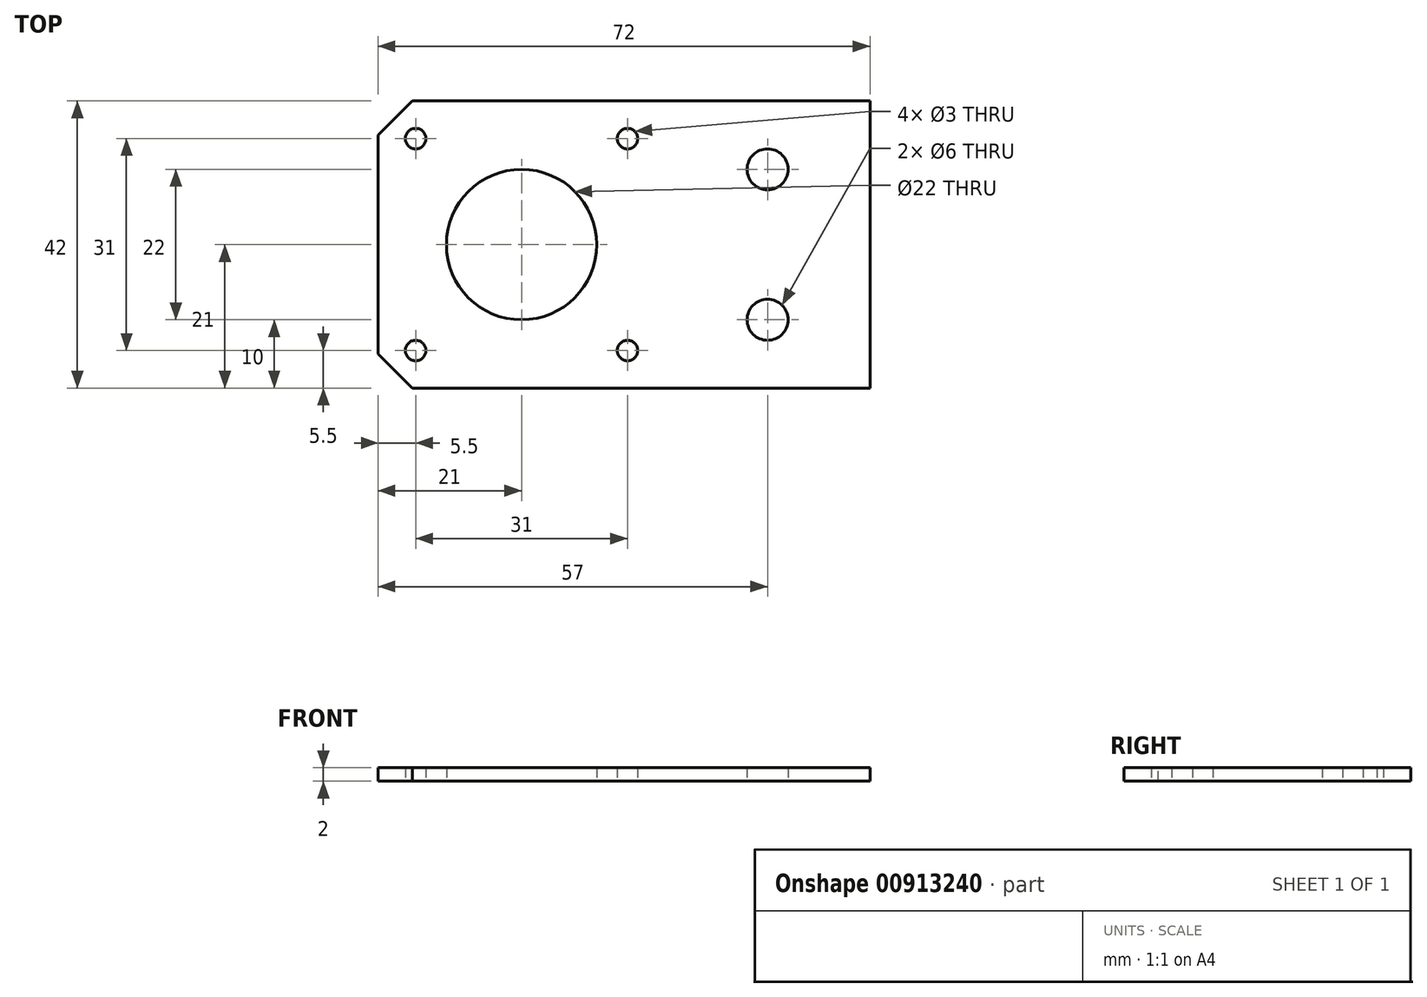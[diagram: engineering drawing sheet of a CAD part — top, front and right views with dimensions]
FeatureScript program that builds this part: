
annotation { "Feature Type Name" : "Feature", "Feature Type Description" : "" }
export const myFeature = defineFeature(function(context is Context, id is Id, definition is map)
    precondition{}
    {
        {
            var Q0;
            Q0=qCreatedBy(makeId("Top.planeOp"),FACE);
            var sketch = newSketch(context, id + "F0", { "sketchPlane" : qUnion([Q0])});
            skLineSegment(sketch, "E0.bottom", {"start": v(36, -21) * mm, "end": v(-36, -21) * mm});
            skLineSegment(sketch, "E0.top", {"start": v(36, 21) * mm, "end": v(-36, 21) * mm});
            skLineSegment(sketch, "E0.left", {"start": v(36, -21) * mm, "end": v(36, 21) * mm});
            skLineSegment(sketch, "E0.right", {"start": v(-36, -21) * mm, "end": v(-36, 21) * mm});
            skPoint(sketch, "E0.middle", {"position": v(0, 0) * mm});
            skCircle(sketch, "E1", {"center": v(21, 11) * mm, "radius": 3 * mm});
            skCircle(sketch, "E2", {"center": v(21, -11) * mm, "radius": 3 * mm});
            skCircle(sketch, "E3", {"center": v(-15, 0) * mm, "radius": 11 * mm});
            skCircle(sketch, "E4", {"center": v(-30.5, 15.5) * mm, "radius": 1.5 * mm});
            skCircle(sketch, "E5", {"center": v(0.5, 15.5) * mm, "radius": 1.5 * mm});
            skCircle(sketch, "E6", {"center": v(0.5, -15.5) * mm, "radius": 1.5 * mm});
            skCircle(sketch, "E7", {"center": v(-30.5, -15.5) * mm, "radius": 1.5 * mm});
            skSolve(sketch);
        }
        {
            var Q0;
            Q0=makeQuery(id+"F0.imprint","IMPRINT",FACE,{"disambiguationData":[TD([[makeQuery(id+"F0.imprint","IMPRINT",EDGE,{"derivedFrom":sQuery(id+"F0.wireOp",EDGE,"E0.bottom")}),-1.0]])]});
            extrude(context, id + "F1", {"entities" : qUnion([Q0]), "depth" : 2 * mm, "offsetDistance" : 25 * mm});
        }
        {
            var Q0;
            Q0=makeQuery(id+"F1.opExtrude","SWEPT_EDGE",EDGE,{"disambiguationData":[OSD([sQuery(id+"F0.wireOp",EDGE,"E0.bottom"),sQuery(id+"F0.wireOp",EDGE,"E0.right")])]});
            var Q1;
            Q1=makeQuery(id+"F1.opExtrude","SWEPT_EDGE",EDGE,{"disambiguationData":[OSD([sQuery(id+"F0.wireOp",EDGE,"E0.top"),sQuery(id+"F0.wireOp",EDGE,"E0.right")])]});
            chamfer(context, id + "F2", {"entities" : qUnion([Q0, Q1]), "width" : 5 * mm, "tangentPropagation" : true});
        }
    });
